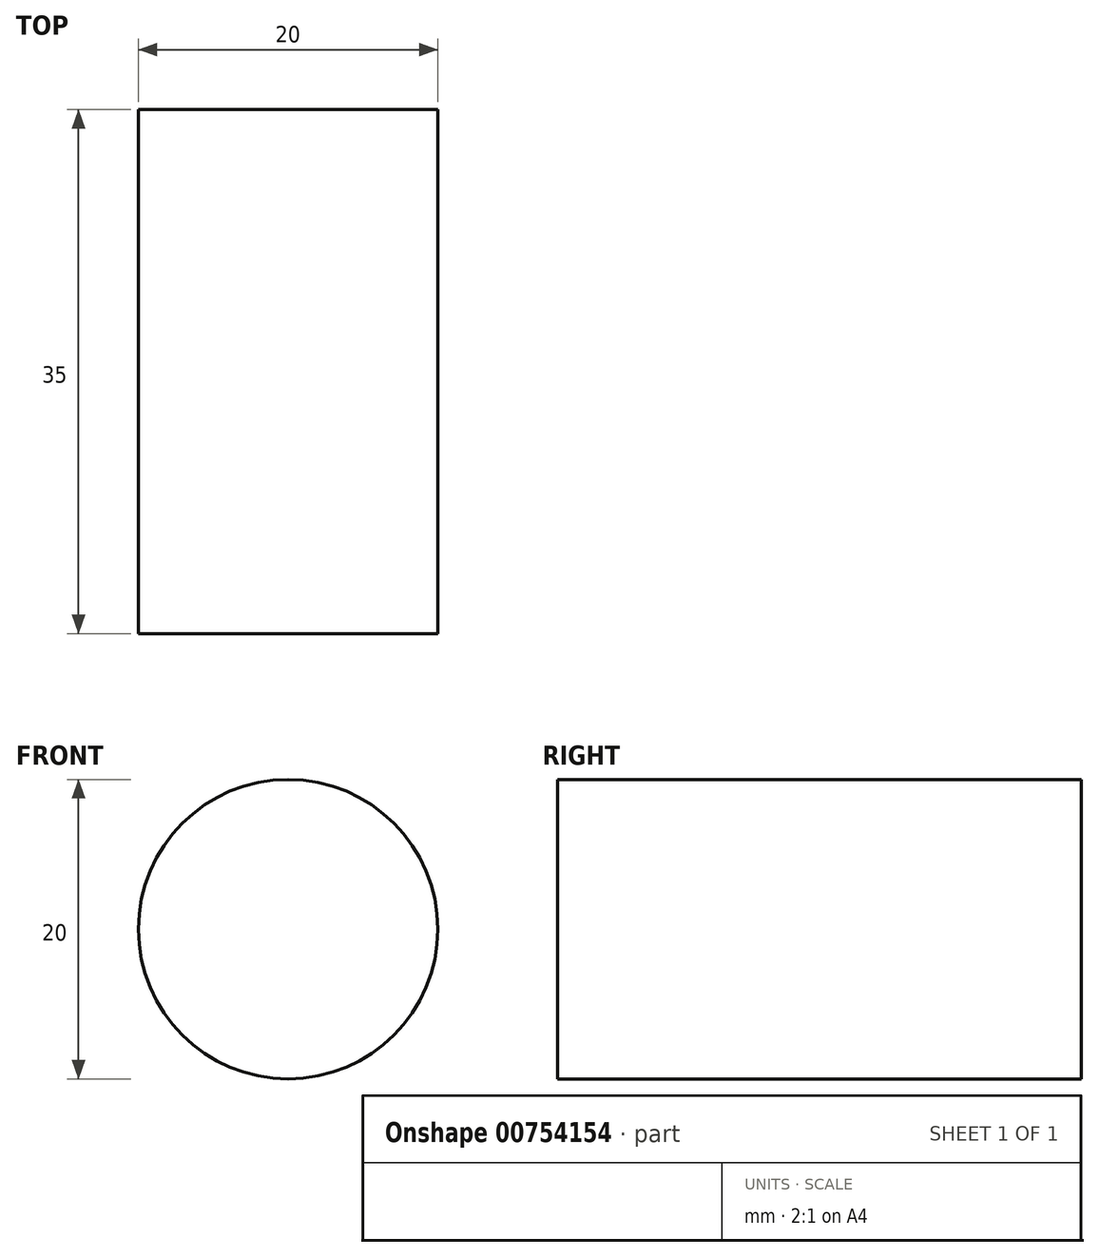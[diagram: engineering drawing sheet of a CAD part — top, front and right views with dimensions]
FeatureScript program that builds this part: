
annotation { "Feature Type Name" : "Feature", "Feature Type Description" : "" }
export const myFeature = defineFeature(function(context is Context, id is Id, definition is map)
    precondition{}
    {
        {
            assignVariable(context, id + "F0", {"name" : "Length", "anyValue" : 35});
        }
        {
            var Q0;
            Q0=qCreatedBy(makeId("Front.planeOp"),FACE);
            var sketch = newSketch(context, id + "F1", { "sketchPlane" : qUnion([Q0])});
            skCircle(sketch, "E0", {"center": v(0, 0) * mm, "radius": 10 * mm});
            skSolve(sketch);
        }
        {
            var Q0;
            Q0=makeQuery(id+"F1.imprint","IMPRINT",FACE,{"disambiguationData":[TD([[makeQuery(id+"F1.imprint","IMPRINT",EDGE,{"derivedFrom":sQuery(id+"F1.wireOp",EDGE,"E0")}),1.0]])]});
            extrude(context, id + "F2", {"entities" : qUnion([Q0]), "oppositeDirection" : true, "depth" : (getVariable(context, 'Length')) * mm, "offsetDistance" : 25 * mm});
        }
    });
